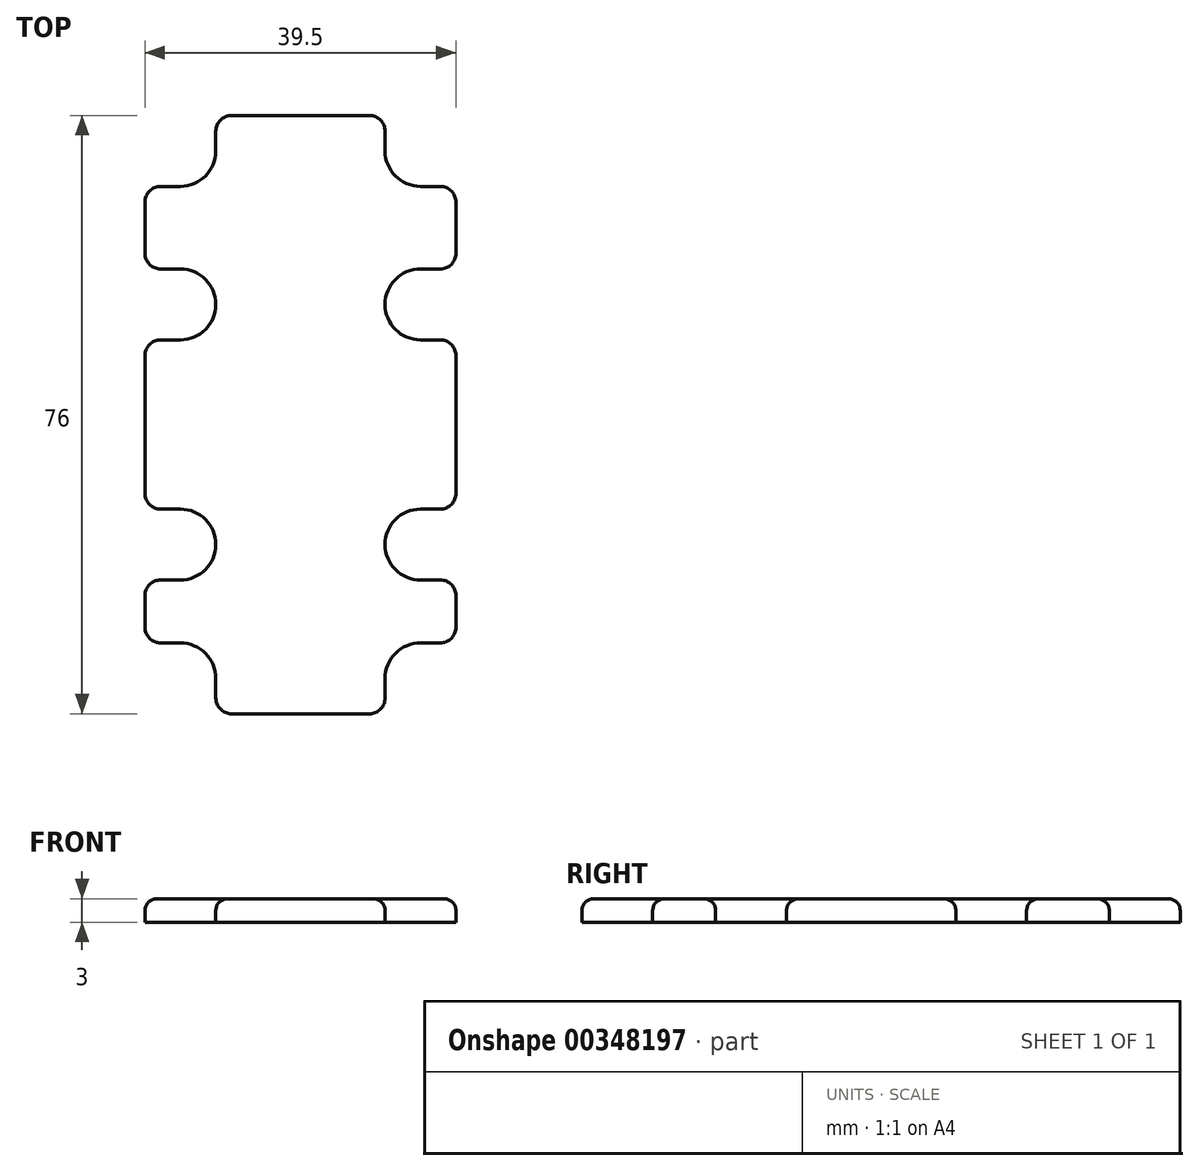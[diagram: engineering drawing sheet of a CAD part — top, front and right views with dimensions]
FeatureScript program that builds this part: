
annotation { "Feature Type Name" : "Feature", "Feature Type Description" : "" }
export const myFeature = defineFeature(function(context is Context, id is Id, definition is map)
    precondition{}
    {
        {
            var Q0;
            Q0=qCreatedBy(makeId("Top.planeOp"),FACE);
            var sketch = newSketch(context, id + "F0", { "sketchPlane" : qUnion([Q0])});
            skPoint(sketch, "E0.middle", {"position": v(0, 0) * mm});
            skPoint(sketch, "E1.endSnap0", {"position": v(15.25, 0) * mm});
            skLineSegment(sketch, "E2", {"start": v(10.75, -32.25) * mm, "end": v(10.75, -36.75) * mm});
            skLineSegment(sketch, "E3", {"start": v(-10.75, -32.25) * mm, "end": v(-10.75, -36.75) * mm});
            skLineSegment(sketch, "E4", {"start": v(-10.75, -36.75) * mm, "end": v(10.75, -36.75) * mm});
            skLineSegment(sketch, "E5", {"start": v(-15.25, -27.75) * mm, "end": v(-19.75, -27.75) * mm});
            skLineSegment(sketch, "E6", {"start": v(-15.25, -19.75) * mm, "end": v(-19.75, -19.75) * mm});
            skLineSegment(sketch, "E7", {"start": v(-19.75, -19.75) * mm, "end": v(-19.75, -27.75) * mm});
            skLineSegment(sketch, "E8", {"start": v(-15.25, -10.75) * mm, "end": v(-19.75, -10.75) * mm});
            skLineSegment(sketch, "E9", {"start": v(-15.25, 10.75) * mm, "end": v(-19.75, 10.75) * mm});
            skLineSegment(sketch, "E10", {"start": v(-19.75, 10.75) * mm, "end": v(-19.75, -10.75) * mm});
            skLineSegment(sketch, "E11", {"start": v(-15.25, 19.75) * mm, "end": v(-19.75, 19.75) * mm});
            skLineSegment(sketch, "E12", {"start": v(-15.25, 30.25) * mm, "end": v(-19.75, 30.25) * mm});
            skLineSegment(sketch, "E13", {"start": v(-19.75, 30.25) * mm, "end": v(-19.75, 19.75) * mm});
            skLineSegment(sketch, "E14", {"start": v(-10.75, 34.75) * mm, "end": v(-10.75, 39.25) * mm});
            skLineSegment(sketch, "E15", {"start": v(10.75, 34.75) * mm, "end": v(10.75, 39.25) * mm});
            skLineSegment(sketch, "E16", {"start": v(10.75, 39.25) * mm, "end": v(-10.75, 39.25) * mm});
            skLineSegment(sketch, "E17", {"start": v(15.25, 30.25) * mm, "end": v(19.75, 30.25) * mm});
            skLineSegment(sketch, "E18", {"start": v(15.25, 19.75) * mm, "end": v(19.75, 19.75) * mm});
            skLineSegment(sketch, "E19", {"start": v(19.75, 19.75) * mm, "end": v(19.75, 30.25) * mm});
            skLineSegment(sketch, "E20", {"start": v(15.25, -19.75) * mm, "end": v(19.75, -19.75) * mm});
            skLineSegment(sketch, "E21", {"start": v(15.25, -27.75) * mm, "end": v(19.75, -27.75) * mm});
            skLineSegment(sketch, "E22", {"start": v(19.75, -27.75) * mm, "end": v(19.75, -19.75) * mm});
            skLineSegment(sketch, "E23", {"start": v(15.25, 10.75) * mm, "end": v(19.75, 10.75) * mm});
            skLineSegment(sketch, "E24", {"start": v(15.25, -10.75) * mm, "end": v(19.75, -10.75) * mm});
            skLineSegment(sketch, "E25", {"start": v(19.75, -10.75) * mm, "end": v(19.75, 10.75) * mm});
            skArc(sketch, "E26", {"start": v(-15.25, 30.25) * mm, "mid": v(-12.07, 31.57) * mm, "end": v(-10.75, 34.75) * mm});
            skArc(sketch, "E27", {"start": v(10.75, 34.75) * mm, "mid": v(12.07, 31.57) * mm, "end": v(15.25, 30.25) * mm});
            skArc(sketch, "E28", {"start": v(-15.25, 10.75) * mm, "mid": v(-10.75, 15.25) * mm, "end": v(-15.25, 19.75) * mm});
            skArc(sketch, "E29", {"start": v(15.25, 19.75) * mm, "mid": v(10.75, 15.25) * mm, "end": v(15.25, 10.75) * mm});
            skArc(sketch, "E30", {"start": v(15.25, -10.75) * mm, "mid": v(10.75, -15.25) * mm, "end": v(15.25, -19.75) * mm});
            skArc(sketch, "E31", {"start": v(15.25, -27.75) * mm, "mid": v(12.07, -29.07) * mm, "end": v(10.75, -32.25) * mm});
            skArc(sketch, "E32", {"start": v(-10.75, -32.25) * mm, "mid": v(-12.07, -29.07) * mm, "end": v(-15.25, -27.75) * mm});
            skArc(sketch, "E33", {"start": v(-15.25, -19.75) * mm, "mid": v(-10.75, -15.25) * mm, "end": v(-15.25, -10.75) * mm});
            skSolve(sketch);
        }
        {
            var Q0;
            Q0=makeQuery(id+"F0.imprint","IMPRINT",FACE,{"disambiguationData":[TD([[makeQuery(id+"F0.imprint","IMPRINT",EDGE,{"derivedFrom":sQuery(id+"F0.wireOp",EDGE,"E2")}),-1.0]])]});
            extrude(context, id + "F1", {"entities" : qUnion([Q0]), "depth" : 3 * mm});
        }
        {
            var Q0;
            Q0=makeQuery(id+"F1.opExtrude","SWEPT_EDGE",EDGE,{"disambiguationData":[OSD([sQuery(id+"F0.wireOp",EDGE,"E21"),sQuery(id+"F0.wireOp",EDGE,"E22")])]});
            var Q1;
            Q1=makeQuery(id+"F1.opExtrude","SWEPT_EDGE",EDGE,{"disambiguationData":[OSD([sQuery(id+"F0.wireOp",EDGE,"E20"),sQuery(id+"F0.wireOp",EDGE,"E22")])]});
            var Q2;
            Q2=makeQuery(id+"F1.opExtrude","SWEPT_EDGE",EDGE,{"disambiguationData":[OSD([sQuery(id+"F0.wireOp",EDGE,"E24"),sQuery(id+"F0.wireOp",EDGE,"E25")])]});
            var Q3;
            Q3=makeQuery(id+"F1.opExtrude","SWEPT_EDGE",EDGE,{"disambiguationData":[OSD([sQuery(id+"F0.wireOp",EDGE,"E23"),sQuery(id+"F0.wireOp",EDGE,"E25")])]});
            var Q4;
            Q4=makeQuery(id+"F1.opExtrude","SWEPT_EDGE",EDGE,{"disambiguationData":[OSD([sQuery(id+"F0.wireOp",EDGE,"E18"),sQuery(id+"F0.wireOp",EDGE,"E19")])]});
            var Q5;
            Q5=makeQuery(id+"F1.opExtrude","SWEPT_EDGE",EDGE,{"disambiguationData":[OSD([sQuery(id+"F0.wireOp",EDGE,"E17"),sQuery(id+"F0.wireOp",EDGE,"E19")])]});
            var Q6;
            Q6=makeQuery(id+"F1.opExtrude","SWEPT_EDGE",EDGE,{"disambiguationData":[OSD([sQuery(id+"F0.wireOp",EDGE,"E15"),sQuery(id+"F0.wireOp",EDGE,"E16")])]});
            var Q7;
            Q7=makeQuery(id+"F1.opExtrude","SWEPT_EDGE",EDGE,{"disambiguationData":[OSD([sQuery(id+"F0.wireOp",EDGE,"E14"),sQuery(id+"F0.wireOp",EDGE,"E16")])]});
            var Q8;
            Q8=makeQuery(id+"F1.opExtrude","SWEPT_EDGE",EDGE,{"disambiguationData":[OSD([sQuery(id+"F0.wireOp",EDGE,"E12"),sQuery(id+"F0.wireOp",EDGE,"E13")])]});
            var Q9;
            Q9=makeQuery(id+"F1.opExtrude","SWEPT_EDGE",EDGE,{"disambiguationData":[OSD([sQuery(id+"F0.wireOp",EDGE,"E11"),sQuery(id+"F0.wireOp",EDGE,"E13")])]});
            var Q10;
            Q10=makeQuery(id+"F1.opExtrude","SWEPT_EDGE",EDGE,{"disambiguationData":[OSD([sQuery(id+"F0.wireOp",EDGE,"E9"),sQuery(id+"F0.wireOp",EDGE,"E10")])]});
            var Q11;
            Q11=makeQuery(id+"F1.opExtrude","SWEPT_EDGE",EDGE,{"disambiguationData":[OSD([sQuery(id+"F0.wireOp",EDGE,"E8"),sQuery(id+"F0.wireOp",EDGE,"E10")])]});
            var Q12;
            Q12=makeQuery(id+"F1.opExtrude","SWEPT_EDGE",EDGE,{"disambiguationData":[OSD([sQuery(id+"F0.wireOp",EDGE,"E5"),sQuery(id+"F0.wireOp",EDGE,"E7")])]});
            var Q13;
            Q13=makeQuery(id+"F1.opExtrude","SWEPT_EDGE",EDGE,{"disambiguationData":[OSD([sQuery(id+"F0.wireOp",EDGE,"E6"),sQuery(id+"F0.wireOp",EDGE,"E7")])]});
            var Q14;
            Q14=makeQuery(id+"F1.opExtrude","SWEPT_EDGE",EDGE,{"disambiguationData":[OSD([sQuery(id+"F0.wireOp",EDGE,"E2"),sQuery(id+"F0.wireOp",EDGE,"E4")])]});
            var Q15;
            Q15=makeQuery(id+"F1.opExtrude","SWEPT_EDGE",EDGE,{"disambiguationData":[OSD([sQuery(id+"F0.wireOp",EDGE,"E3"),sQuery(id+"F0.wireOp",EDGE,"E4")])]});
            fillet(context, id + "F2", {"entities" : qUnion([Q0, Q1, Q2, Q3, Q4, Q5, Q6, Q7, Q8, Q9, Q10, Q11, Q12, Q13, Q14, Q15]), "radius" : 2 * mm, "tangentPropagation" : true, "allowEdgeOverflow" : false});
        }
        {
            var Q0;
            Q0=makeQuery(id+"F1.opExtrude","CAP_FACE",FACE,{"disambiguationData":[OSD([sQuery(id+"F0.wireOp",EDGE,"E2"),sQuery(id+"F0.wireOp",EDGE,"E3"),sQuery(id+"F0.wireOp",EDGE,"E4"),sQuery(id+"F0.wireOp",EDGE,"E5"),sQuery(id+"F0.wireOp",EDGE,"E6"),sQuery(id+"F0.wireOp",EDGE,"E7"),sQuery(id+"F0.wireOp",EDGE,"E8"),sQuery(id+"F0.wireOp",EDGE,"E9"),sQuery(id+"F0.wireOp",EDGE,"E10"),sQuery(id+"F0.wireOp",EDGE,"E11"),sQuery(id+"F0.wireOp",EDGE,"E12"),sQuery(id+"F0.wireOp",EDGE,"E13"),sQuery(id+"F0.wireOp",EDGE,"E14"),sQuery(id+"F0.wireOp",EDGE,"E15"),sQuery(id+"F0.wireOp",EDGE,"E16"),sQuery(id+"F0.wireOp",EDGE,"E17"),sQuery(id+"F0.wireOp",EDGE,"E18"),sQuery(id+"F0.wireOp",EDGE,"E19"),sQuery(id+"F0.wireOp",EDGE,"E20"),sQuery(id+"F0.wireOp",EDGE,"E21"),sQuery(id+"F0.wireOp",EDGE,"E22"),sQuery(id+"F0.wireOp",EDGE,"E23"),sQuery(id+"F0.wireOp",EDGE,"E24"),sQuery(id+"F0.wireOp",EDGE,"E25"),sQuery(id+"F0.wireOp",EDGE,"E26"),sQuery(id+"F0.wireOp",EDGE,"E27"),sQuery(id+"F0.wireOp",EDGE,"E29"),sQuery(id+"F0.wireOp",EDGE,"E30"),sQuery(id+"F0.wireOp",EDGE,"E31"),sQuery(id+"F0.wireOp",EDGE,"E32"),sQuery(id+"F0.wireOp",EDGE,"E28"),sQuery(id+"F0.wireOp",EDGE,"E33")])],"isStart":false});
            fillet(context, id + "F3", {"entities" : qUnion([Q0]), "radius" : 1.5 * mm, "tangentPropagation" : true, "allowEdgeOverflow" : false});
        }
    });
